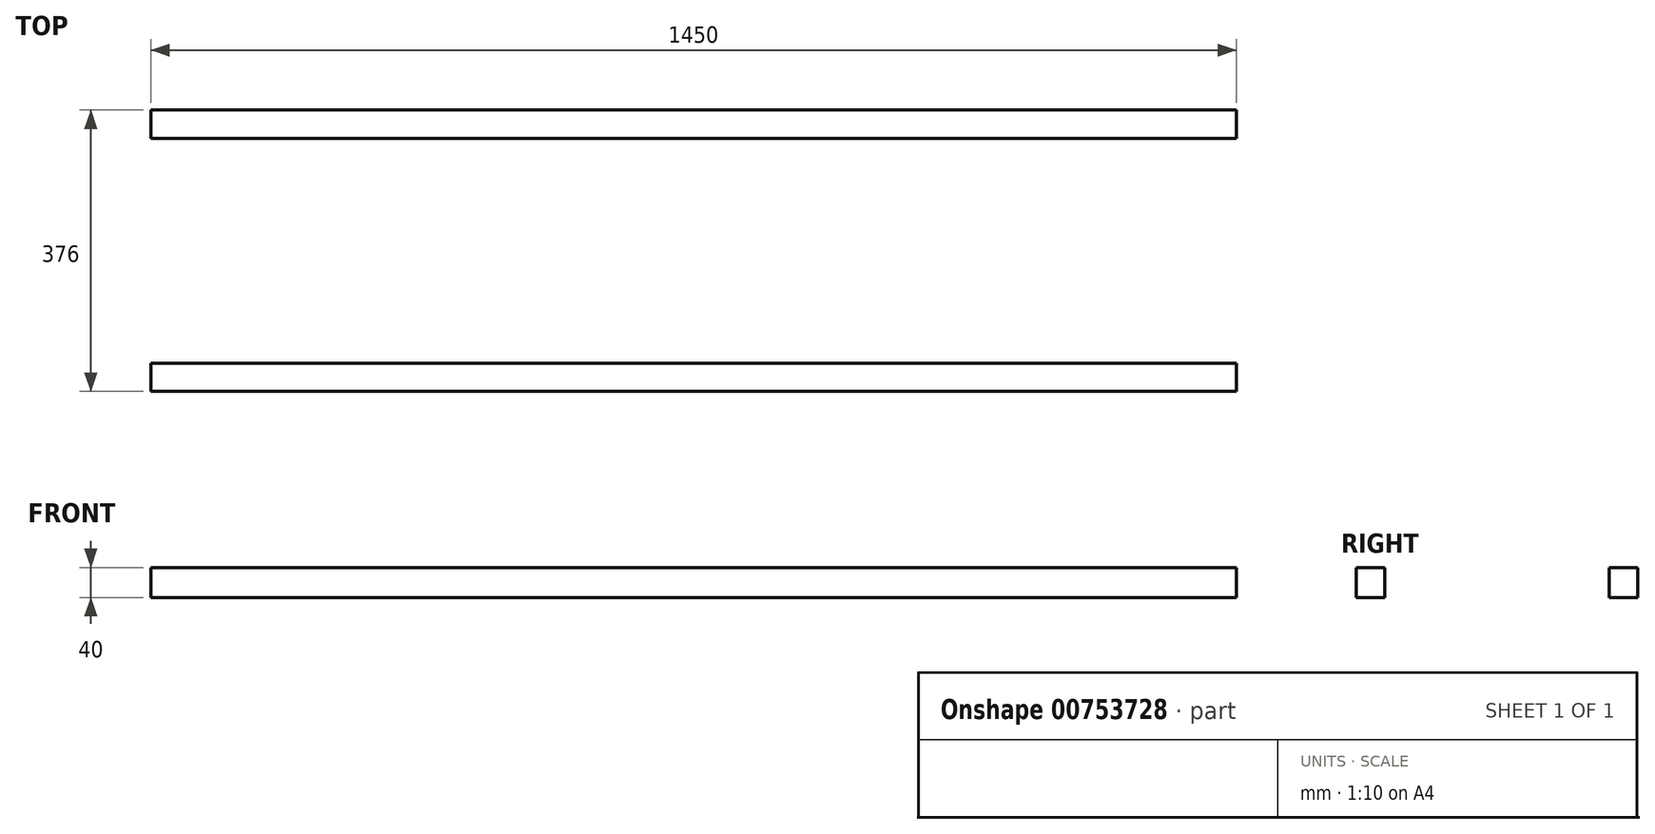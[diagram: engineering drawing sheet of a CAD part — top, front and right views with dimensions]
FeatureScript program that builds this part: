
annotation { "Feature Type Name" : "Feature", "Feature Type Description" : "" }
export const myFeature = defineFeature(function(context is Context, id is Id, definition is map)
    precondition{}
    {
        {
            var Q0;
            Q0=qCreatedBy(makeId("Top.planeOp"),FACE);
            var sketch = newSketch(context, id + "F0", { "sketchPlane" : qUnion([Q0])});
            skLineSegment(sketch, "E0.bottom", {"start": v(-669.51, -229.4) * mm, "end": v(780.49, -229.4) * mm});
            skLineSegment(sketch, "E0.top", {"start": v(-669.51, -191.4) * mm, "end": v(780.49, -191.4) * mm});
            skLineSegment(sketch, "E0.left", {"start": v(-669.51, -229.4) * mm, "end": v(-669.51, -191.4) * mm});
            skLineSegment(sketch, "E0.right", {"start": v(780.49, -229.4) * mm, "end": v(780.49, -191.4) * mm});
            skLineSegment(sketch, "E1.bottom", {"start": v(-669.51, 108.6) * mm, "end": v(780.49, 108.6) * mm});
            skLineSegment(sketch, "E1.top", {"start": v(-669.51, 146.6) * mm, "end": v(780.49, 146.6) * mm});
            skLineSegment(sketch, "E1.left", {"start": v(-669.51, 108.6) * mm, "end": v(-669.51, 146.6) * mm});
            skLineSegment(sketch, "E1.right", {"start": v(780.49, 108.6) * mm, "end": v(780.49, 146.6) * mm});
            skSolve(sketch);
        }
        {
            var Q0;
            Q0=makeQuery(id+"F0.imprint","IMPRINT",FACE,{"disambiguationData":[TD([[makeQuery(id+"F0.imprint","IMPRINT",EDGE,{"derivedFrom":sQuery(id+"F0.wireOp",EDGE,"E0.bottom")}),1.0]])]});
            var Q1;
            Q1=makeQuery(id+"F0.imprint","IMPRINT",FACE,{"disambiguationData":[TD([[makeQuery(id+"F0.imprint","IMPRINT",EDGE,{"derivedFrom":sQuery(id+"F0.wireOp",EDGE,"E1.bottom")}),1.0]])]});
            extrude(context, id + "F1", {"entities" : qUnion([Q0, Q1]), "depth" : 40 * mm, "offsetDistance" : 25 * mm});
        }
    });
